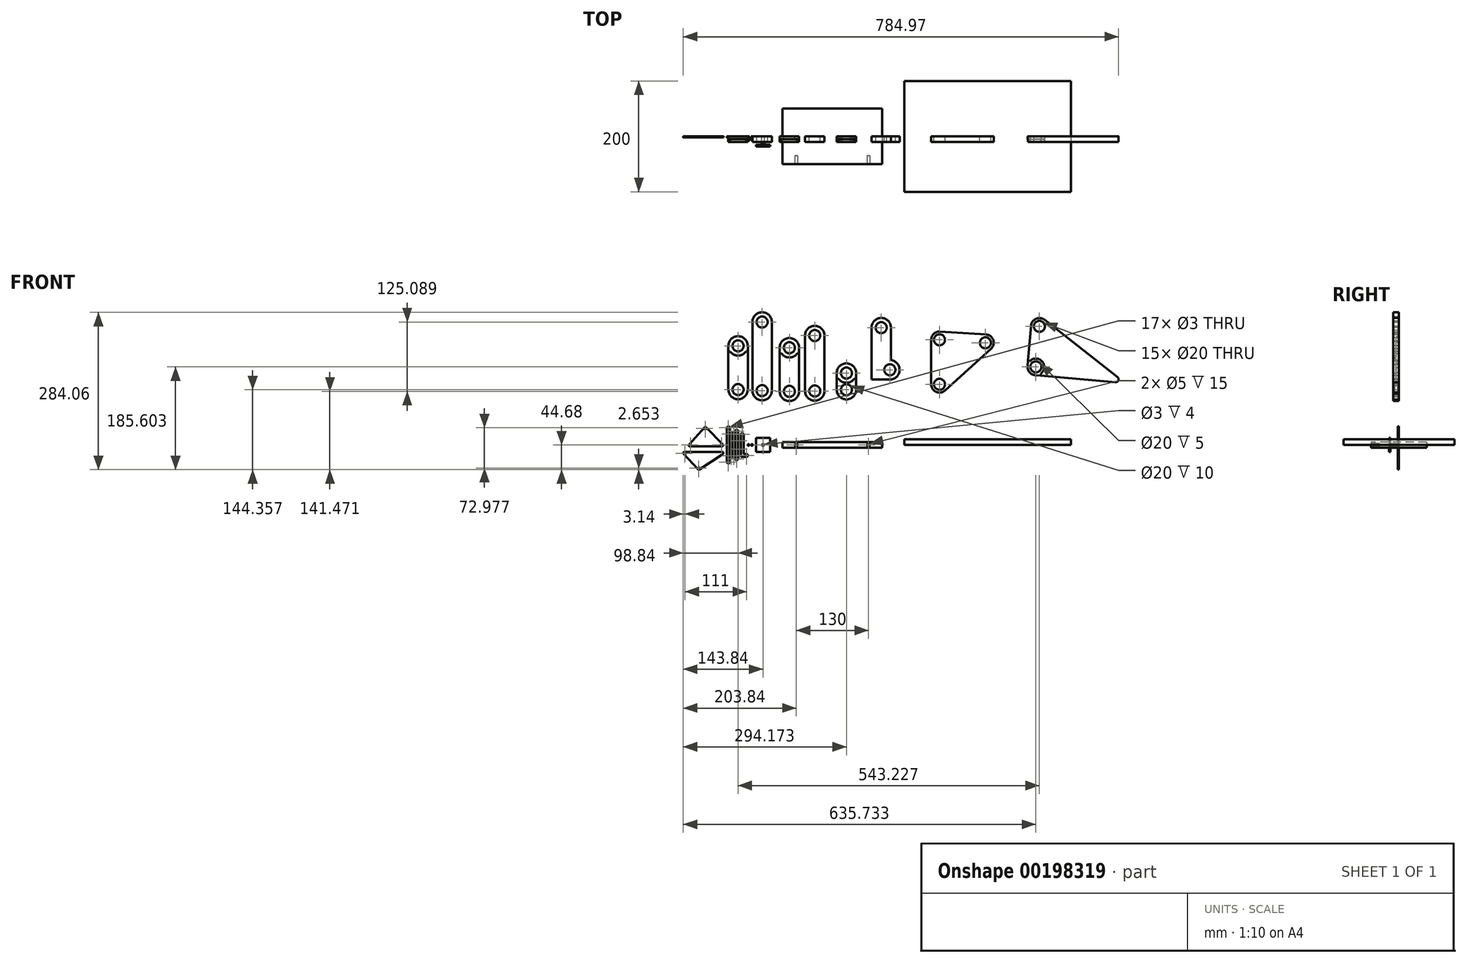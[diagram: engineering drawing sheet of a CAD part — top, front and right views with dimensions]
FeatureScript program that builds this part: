
annotation { "Feature Type Name" : "Feature", "Feature Type Description" : "" }
export const myFeature = defineFeature(function(context is Context, id is Id, definition is map)
    precondition{}
    {
        {
            var Q0;
            Q0=qCreatedBy(makeId("Front.planeOp"),FACE);
            var sketch = newSketch(context, id + "F0", { "sketchPlane" : qUnion([Q0])});
            skLineSegment(sketch, "E0", {"start": v(0, 7.5) * mm, "end": v(0, -7.5) * mm});
            skLineSegment(sketch, "E1", {"start": v(5, 7.5) * mm, "end": v(5, -7.5) * mm});
            skArc(sketch, "E2", {"start": v(5, 7.5) * mm, "mid": v(2.5, 10) * mm, "end": v(0, 7.5) * mm});
            skArc(sketch, "E3", {"start": v(0, -7.5) * mm, "mid": v(2.5, -10) * mm, "end": v(5, -7.5) * mm});
            skCircle(sketch, "E4", {"center": v(2.5, 7.5) * mm, "radius": 1.5 * mm});
            skCircle(sketch, "E5", {"center": v(2.5, -7.5) * mm, "radius": 1.5 * mm});
            skSolve(sketch);
        }
        {
            var Q0;
            Q0=makeQuery(id+"F0.imprint","IMPRINT",FACE,{"disambiguationData":[TD([[makeQuery(id+"F0.imprint","IMPRINT",EDGE,{"derivedFrom":sQuery(id+"F0.wireOp",EDGE,"E0")}),1.0]])]});
            extrude(context, id + "F1", {"entities" : qUnion([Q0]), "depth" : 2 * mm});
        }
        {
            var Q0;
            Q0=qCreatedBy(makeId("Front.planeOp"),FACE);
            var sketch = newSketch(context, id + "F2", { "sketchPlane" : qUnion([Q0])});
            skLineSegment(sketch, "E6", {"start": v(0, 25) * mm, "end": v(0, -25) * mm});
            skLineSegment(sketch, "E7", {"start": v(-5, 25) * mm, "end": v(-5, -25) * mm});
            skArc(sketch, "E8", {"start": v(0, 25) * mm, "mid": v(-2.5, 27.5) * mm, "end": v(-5, 25) * mm});
            skArc(sketch, "E9", {"start": v(-5, -25) * mm, "mid": v(-2.5, -27.5) * mm, "end": v(0, -25) * mm});
            skCircle(sketch, "E10", {"center": v(-2.5, 25) * mm, "radius": 1.5 * mm});
            skCircle(sketch, "E11", {"center": v(-2.5, -25) * mm, "radius": 1.5 * mm});
            skSolve(sketch);
        }
        {
            var Q0;
            Q0=makeQuery(id+"F2.imprint","IMPRINT",FACE,{"disambiguationData":[TD([[makeQuery(id+"F2.imprint","IMPRINT",EDGE,{"derivedFrom":sQuery(id+"F2.wireOp",EDGE,"E6")}),-1.0]])]});
            extrude(context, id + "F3", {"entities" : qUnion([Q0]), "depth" : 2 * mm});
        }
        {
            var Q0;
            Q0=qCreatedBy(makeId("Front.planeOp"),FACE);
            var sketch = newSketch(context, id + "F4", { "sketchPlane" : qUnion([Q0])});
            skLineSegment(sketch, "E12", {"start": v(-5, 19.65) * mm, "end": v(-5, -19.65) * mm});
            skLineSegment(sketch, "E13", {"start": v(-10, 19.65) * mm, "end": v(-10, -19.65) * mm});
            skArc(sketch, "E14", {"start": v(-5, 19.65) * mm, "mid": v(-7.5, 22.15) * mm, "end": v(-10, 19.65) * mm});
            skArc(sketch, "E15", {"start": v(-10, -19.65) * mm, "mid": v(-7.5, -22.15) * mm, "end": v(-5, -19.65) * mm});
            skCircle(sketch, "E16", {"center": v(-7.5, 19.65) * mm, "radius": 1.5 * mm});
            skCircle(sketch, "E17", {"center": v(-7.5, -19.65) * mm, "radius": 1.5 * mm});
            skSolve(sketch);
        }
        {
            var Q0;
            Q0=makeQuery(id+"F4.imprint","IMPRINT",FACE,{"disambiguationData":[TD([[makeQuery(id+"F4.imprint","IMPRINT",EDGE,{"derivedFrom":sQuery(id+"F4.wireOp",EDGE,"E12")}),-1.0]])]});
            extrude(context, id + "F5", {"entities" : qUnion([Q0]), "depth" : 2 * mm});
        }
        {
            var Q0;
            Q0=qCreatedBy(makeId("Front.planeOp"),FACE);
            var sketch = newSketch(context, id + "F6", { "sketchPlane" : qUnion([Q0])});
            skLineSegment(sketch, "E18", {"start": v(-10, 19.7) * mm, "end": v(-10, -19.7) * mm});
            skLineSegment(sketch, "E19", {"start": v(-15, 19.7) * mm, "end": v(-15, -19.7) * mm});
            skArc(sketch, "E20", {"start": v(-10, 19.7) * mm, "mid": v(-12.5, 22.2) * mm, "end": v(-15, 19.7) * mm});
            skArc(sketch, "E21", {"start": v(-15, -19.7) * mm, "mid": v(-12.5, -22.2) * mm, "end": v(-10, -19.7) * mm});
            skCircle(sketch, "E22", {"center": v(-12.5, 19.7) * mm, "radius": 1.5 * mm});
            skCircle(sketch, "E23", {"center": v(-12.5, -19.7) * mm, "radius": 1.5 * mm});
            skSolve(sketch);
        }
        {
            var Q0;
            Q0=makeQuery(id+"F6.imprint","IMPRINT",FACE,{"disambiguationData":[TD([[makeQuery(id+"F6.imprint","IMPRINT",EDGE,{"derivedFrom":sQuery(id+"F6.wireOp",EDGE,"E18")}),-1.0]])]});
            extrude(context, id + "F7", {"entities" : qUnion([Q0]), "depth" : 2 * mm});
        }
        {
            var Q0;
            Q0=qCreatedBy(makeId("Front.planeOp"),FACE);
            var sketch = newSketch(context, id + "F8", { "sketchPlane" : qUnion([Q0])});
            skLineSegment(sketch, "E24", {"start": v(-20, 30.95) * mm, "end": v(-20, -30.95) * mm});
            skLineSegment(sketch, "E25", {"start": v(-15, 30.95) * mm, "end": v(-15, -30.95) * mm});
            skArc(sketch, "E26", {"start": v(-15, 30.95) * mm, "mid": v(-17.5, 33.45) * mm, "end": v(-20, 30.95) * mm});
            skArc(sketch, "E27", {"start": v(-20, -30.95) * mm, "mid": v(-17.5, -33.45) * mm, "end": v(-15, -30.95) * mm});
            skCircle(sketch, "E28", {"center": v(-17.5, -30.95) * mm, "radius": 1.5 * mm});
            skCircle(sketch, "E29", {"center": v(-17.5, 30.95) * mm, "radius": 1.5 * mm});
            skSolve(sketch);
        }
        {
            var Q0;
            Q0=makeQuery(id+"F8.imprint","IMPRINT",FACE,{"disambiguationData":[TD([[makeQuery(id+"F8.imprint","IMPRINT",EDGE,{"derivedFrom":sQuery(id+"F8.wireOp",EDGE,"E24")}),1.0]])]});
            extrude(context, id + "F9", {"entities" : qUnion([Q0]), "depth" : 2 * mm});
        }
        {
            var Q0;
            Q0=qCreatedBy(makeId("Front.planeOp"),FACE);
            var sketch = newSketch(context, id + "F10", { "sketchPlane" : qUnion([Q0])});
            skLineSegment(sketch, "E30", {"start": v(-58.92, 29.76) * mm, "end": v(-30, 0) * mm, "construction": true});
            skLineSegment(sketch, "E31", {"start": v(-30, 0) * mm, "end": v(-85.8, 0) * mm, "construction": true});
            skLineSegment(sketch, "E32", {"start": v(-85.8, 0) * mm, "end": v(-58.92, 29.76) * mm, "construction": true});
            skCircle(sketch, "E33", {"center": v(-85.8, 0) * mm, "radius": 1.5 * mm});
            skCircle(sketch, "E34", {"center": v(-30, 0) * mm, "radius": 1.5 * mm});
            skCircle(sketch, "E35", {"center": v(-58.92, 29.76) * mm, "radius": 1.5 * mm});
            skLineSegment(sketch, "E36", {"start": v(-91.43, -2.5) * mm, "end": v(-24.08, -2.5) * mm});
            skLineSegment(sketch, "E37", {"start": v(-59, 33.42) * mm, "end": v(-91.43, -2.5) * mm});
            skLineSegment(sketch, "E38", {"start": v(-59, 33.42) * mm, "end": v(-24.08, -2.5) * mm});
            skSolve(sketch);
        }
        {
            var Q0;
            Q0=makeQuery(id+"F10.imprint","IMPRINT",FACE,{"disambiguationData":[TD([[makeQuery(id+"F10.imprint","IMPRINT",EDGE,{"derivedFrom":sQuery(id+"F10.wireOp",EDGE,"E33")}),-1.0]])]});
            extrude(context, id + "F11", {"entities" : qUnion([Q0]), "depth" : 2 * mm});
        }
        {
            var Q0;
            Q0=makeQuery(id+"F11.opExtrude","SWEPT_EDGE",EDGE,{"disambiguationData":[OSD([sQuery(id+"F10.wireOp",EDGE,"E36"),sQuery(id+"F10.wireOp",EDGE,"E37")])]});
            var Q1;
            Q1=makeQuery(id+"F11.opExtrude","SWEPT_EDGE",EDGE,{"disambiguationData":[OSD([sQuery(id+"F10.wireOp",EDGE,"E36"),sQuery(id+"F10.wireOp",EDGE,"E38")])]});
            var Q2;
            Q2=makeQuery(id+"F11.opExtrude","SWEPT_EDGE",EDGE,{"disambiguationData":[OSD([sQuery(id+"F10.wireOp",EDGE,"E37"),sQuery(id+"F10.wireOp",EDGE,"E38")])]});
            fillet(context, id + "F12", {"entities" : qUnion([Q0, Q1, Q2]), "radius" : 2 * mm, "tangentPropagation" : true, "allowEdgeOverflow" : false});
        }
        {
            var Q0;
            Q0=qCreatedBy(makeId("Front.planeOp"),FACE);
            var sketch = newSketch(context, id + "F13", { "sketchPlane" : qUnion([Q0])});
            skLineSegment(sketch, "E39", {"start": v(-95.7, -15) * mm, "end": v(-30, -15) * mm, "construction": true});
            skLineSegment(sketch, "E40", {"start": v(-30, -15) * mm, "end": v(-70.87, -42.03) * mm, "construction": true});
            skLineSegment(sketch, "E41", {"start": v(-70.87, -42.03) * mm, "end": v(-95.7, -15) * mm, "construction": true});
            skCircle(sketch, "E42", {"center": v(-95.7, -15) * mm, "radius": 1.5 * mm});
            skCircle(sketch, "E43", {"center": v(-70.87, -42.03) * mm, "radius": 1.5 * mm});
            skLineSegment(sketch, "E44", {"start": v(-101.4, -12.5) * mm, "end": v(-21.69, -12.5) * mm});
            skLineSegment(sketch, "E45", {"start": v(-21.69, -12.5) * mm, "end": v(-71.27, -45.29) * mm});
            skLineSegment(sketch, "E46", {"start": v(-71.27, -45.29) * mm, "end": v(-101.4, -12.5) * mm});
            skSolve(sketch);
        }
        {
            var Q0;
            Q0=makeQuery(id+"F13.imprint","IMPRINT",FACE,{"disambiguationData":[TD([[makeQuery(id+"F13.imprint","IMPRINT",EDGE,{"derivedFrom":sQuery(id+"F13.wireOp",EDGE,"E42")}),-1.0]])]});
            extrude(context, id + "F14", {"entities" : qUnion([Q0]), "depth" : 2 * mm});
        }
        {
            var Q0;
            Q0=makeQuery(id+"F14.opExtrude","SWEPT_EDGE",EDGE,{"disambiguationData":[OSD([sQuery(id+"F13.wireOp",EDGE,"E44"),sQuery(id+"F13.wireOp",EDGE,"E46")])]});
            var Q1;
            Q1=makeQuery(id+"F14.opExtrude","SWEPT_EDGE",EDGE,{"disambiguationData":[OSD([sQuery(id+"F13.wireOp",EDGE,"E45"),sQuery(id+"F13.wireOp",EDGE,"E46")])]});
            var Q2;
            Q2=makeQuery(id+"F14.opExtrude","SWEPT_EDGE",EDGE,{"disambiguationData":[OSD([sQuery(id+"F13.wireOp",EDGE,"E44"),sQuery(id+"F13.wireOp",EDGE,"E45")])]});
            fillet(context, id + "F15", {"entities" : qUnion([Q0, Q1, Q2]), "radius" : 2 * mm, "tangentPropagation" : true, "allowEdgeOverflow" : false});
        }
        {
            var Q0;
            Q0=qCreatedBy(makeId("Front.planeOp"),FACE);
            var sketch = newSketch(context, id + "F16", { "sketchPlane" : qUnion([Q0])});
            skLineSegment(sketch, "E47", {"start": v(7.5, 19) * mm, "end": v(7.5, -19) * mm, "construction": true});
            skLineSegment(sketch, "E48", {"start": v(7.5, -19) * mm, "end": v(15.3, -19) * mm, "construction": true});
            skArc(sketch, "E49", {"start": v(10, 19) * mm, "mid": v(7.5, 21.5) * mm, "end": v(5, 19) * mm});
            skArc(sketch, "E50", {"start": v(15.3, -21.5) * mm, "mid": v(17.8, -19) * mm, "end": v(15.3, -16.5) * mm});
            skLineSegment(sketch, "E51", {"start": v(5, 19) * mm, "end": v(5, -21.5) * mm});
            skLineSegment(sketch, "E52", {"start": v(15.3, -21.5) * mm, "end": v(5, -21.5) * mm});
            skLineSegment(sketch, "E53", {"start": v(10, 19) * mm, "end": v(10, -16.5) * mm});
            skLineSegment(sketch, "E54", {"start": v(15.3, -16.5) * mm, "end": v(10, -16.5) * mm});
            skCircle(sketch, "E55", {"center": v(7.5, 19) * mm, "radius": 1.5 * mm});
            skCircle(sketch, "E56", {"center": v(15.3, -19) * mm, "radius": 1.5 * mm});
            skSolve(sketch);
        }
        {
            var Q0;
            Q0=makeQuery(id+"F16.imprint","IMPRINT",FACE,{"disambiguationData":[TD([[makeQuery(id+"F16.imprint","IMPRINT",EDGE,{"derivedFrom":sQuery(id+"F16.wireOp",EDGE,"E49")}),1.0]])]});
            extrude(context, id + "F17", {"entities" : qUnion([Q0]), "depth" : 2 * mm});
        }
        {
            var Q0;
            Q0=qCreatedBy(makeId("Front.planeOp"),FACE);
            var sketch = newSketch(context, id + "F18", { "sketchPlane" : qUnion([Q0])});
            skCircle(sketch, "E57", {"center": v(24.95, 0) * mm, "radius": 1.5 * mm});
            skSolve(sketch);
        }
        {
            var Q0;
            Q0=makeQuery(id+"F18.imprint","IMPRINT",FACE,{"disambiguationData":[TD([[makeQuery(id+"F18.imprint","IMPRINT",EDGE,{"derivedFrom":sQuery(id+"F18.wireOp",EDGE,"E57")}),1.0]])]});
            extrude(context, id + "F19", {"entities" : qUnion([Q0]), "depth" : 6 * mm});
        }
        {
            var Q0;
            Q0=qCreatedBy(makeId("Front.planeOp"),FACE);
            var sketch = newSketch(context, id + "F20", { "sketchPlane" : qUnion([Q0])});
            skCircle(sketch, "E58", {"center": v(45, 0) * mm, "radius": 2.5 * mm});
            skSolve(sketch);
        }
        {
            var Q0;
            Q0=makeQuery(id+"F20.imprint","IMPRINT",FACE,{"disambiguationData":[TD([[makeQuery(id+"F20.imprint","IMPRINT",EDGE,{"derivedFrom":sQuery(id+"F20.wireOp",EDGE,"E58")}),1.0]])]});
            extrude(context, id + "F21", {"entities" : qUnion([Q0]), "depth" : 15 * mm, "offsetDistance" : 25 * mm});
        }
        {
            var Q0;
            Q0=makeQuery(id+"F21.opExtrude","CAP_FACE",FACE,{"disambiguationData":[OSD([sQuery(id+"F20.wireOp",EDGE,"E58")])],"isStart":false});
            var sketch = newSketch(context, id + "F22", { "sketchPlane" : qUnion([Q0])});
            skLineSegment(sketch, "E59.bottom", {"start": v(32.5, 12.5) * mm, "end": v(57.5, 12.5) * mm});
            skLineSegment(sketch, "E59.top", {"start": v(32.5, -12.5) * mm, "end": v(57.5, -12.5) * mm});
            skLineSegment(sketch, "E59.left", {"start": v(32.5, 12.5) * mm, "end": v(32.5, -12.5) * mm});
            skLineSegment(sketch, "E59.right", {"start": v(57.5, 12.5) * mm, "end": v(57.5, -12.5) * mm});
            skCircle(sketch, "E60.0", {"center": v(45, 0) * mm, "radius": 2.5 * mm, "construction": true});
            skSolve(sketch);
        }
        {
            var Q0;
            Q0=makeQuery(id+"F22.imprint","IMPRINT",FACE,{"disambiguationData":[TD([[makeQuery(id+"F22.imprint","IMPRINT",EDGE,{"derivedFrom":sQuery(id+"F22.wireOp",EDGE,"E59.bottom")}),-1.0]])]});
            var Q1;
            Q1=makeQuery(id+"F22.imprint","IMPRINT",FACE,{"disambiguationData":[TD([[makeQuery(id+"F22.imprint","IMPRINT",EDGE,{"derivedFrom":makeQuery(id+"F21.opExtrude","CAP_EDGE",EDGE,{"disambiguationData":[OSD([sQuery(id+"F20.wireOp",EDGE,"E58")])],"isStart":false})}),1.0]])]});
            extrude(context, id + "F23", {"entities" : qUnion([Q0, Q1]), "operationType" : NewBodyOperationType.ADD, "depth" : 3 * mm});
        }
        {
            var Q0;
            Q0=makeQuery(id+"F23.opExtrude","CAP_FACE",FACE,{"disambiguationData":[OSD([sQuery(id+"F22.wireOp",EDGE,"E59.bottom"),sQuery(id+"F22.wireOp",EDGE,"E59.top"),sQuery(id+"F22.wireOp",EDGE,"E59.left"),sQuery(id+"F22.wireOp",EDGE,"E59.right")])],"isStart":false});
            var sketch = newSketch(context, id + "F24", { "sketchPlane" : qUnion([Q0])});
            skCircle(sketch, "E61", {"center": v(45, 0) * mm, "radius": 1.5 * mm});
            skSolve(sketch);
        }
        {
            var Q0;
            Q0=makeQuery(id+"F24.imprint","IMPRINT",FACE,{"disambiguationData":[TD([[makeQuery(id+"F24.imprint","IMPRINT",EDGE,{"derivedFrom":sQuery(id+"F24.wireOp",EDGE,"E61")}),1.0]])]});
            extrude(context, id + "F25", {"entities" : qUnion([Q0]), "operationType" : NewBodyOperationType.REMOVE, "oppositeDirection" : true, "depth" : 4 * mm});
        }
        {
            var Q0;
            Q0=qCreatedBy(makeId("Front.planeOp"),FACE);
            var sketch = newSketch(context, id + "F26", { "sketchPlane" : qUnion([Q0])});
            skCircle(sketch, "E62", {"center": v(18.95, 0) * mm, "radius": 1.5 * mm});
            skSolve(sketch);
        }
        {
            var Q0;
            Q0=makeQuery(id+"F26.imprint","IMPRINT",FACE,{"disambiguationData":[TD([[makeQuery(id+"F26.imprint","IMPRINT",EDGE,{"derivedFrom":sQuery(id+"F26.wireOp",EDGE,"E62")}),1.0]])]});
            extrude(context, id + "F27", {"entities" : qUnion([Q0]), "depth" : 8 * mm});
        }
        {
            var Q0;
            Q0=qCreatedBy(makeId("Top.planeOp"),FACE);
            var sketch = newSketch(context, id + "F28", { "sketchPlane" : qUnion([Q0])});
            skLineSegment(sketch, "E63.bottom", {"start": v(80, 50) * mm, "end": v(260, 50) * mm});
            skLineSegment(sketch, "E63.top", {"start": v(80, -50) * mm, "end": v(260, -50) * mm});
            skLineSegment(sketch, "E63.left", {"start": v(80, 50) * mm, "end": v(80, -50) * mm});
            skLineSegment(sketch, "E63.right", {"start": v(260, 50) * mm, "end": v(260, -50) * mm});
            skSolve(sketch);
        }
        {
            var Q0;
            Q0 = qSketchRegion(id + "F28", true);
            extrude(context, id + "F29", {"entities" : qUnion([Q0]), "depth" : 5 * mm, "offsetDistance" : 25 * mm, "hasSecondDirection" : true, "secondDirectionOppositeDirection" : true, "secondDirectionDepth" : 5 * mm});
        }
        {
            var Q0;
            Q0=makeQuery(id+"F29.opExtrude","SWEPT_FACE",FACE,{"disambiguationData":[OSD([sQuery(id+"F28.wireOp",EDGE,"E63.top")])]});
            var sketch = newSketch(context, id + "F30", { "sketchPlane" : qUnion([Q0])});
            skCircle(sketch, "E64", {"center": v(105, 0) * mm, "radius": 2.5 * mm});
            skPoint(sketch, "E64.centerSnap0", {"position": v(80, 0) * mm});
            skCircle(sketch, "E65", {"center": v(235, 0) * mm, "radius": 2.5 * mm});
            skSolve(sketch);
        }
        {
            var Q0;
            Q0 = qSketchRegion(id + "F30", true);
            extrude(context, id + "F31", {"entities" : qUnion([Q0]), "operationType" : NewBodyOperationType.REMOVE, "oppositeDirection" : true, "depth" : 15 * mm, "offsetDistance" : 25 * mm});
        }
        {
            var Q0;
            Q0=qCreatedBy(makeId("Top.planeOp"),FACE);
            var sketch = newSketch(context, id + "F32", { "sketchPlane" : qUnion([Q0])});
            skLineSegment(sketch, "E66.bottom", {"start": v(300, 100) * mm, "end": v(600, 100) * mm});
            skLineSegment(sketch, "E66.top", {"start": v(300, -100) * mm, "end": v(600, -100) * mm});
            skLineSegment(sketch, "E66.left", {"start": v(300, 100) * mm, "end": v(300, -100) * mm});
            skLineSegment(sketch, "E66.right", {"start": v(600, 100) * mm, "end": v(600, -100) * mm});
            skSolve(sketch);
        }
        {
            var Q0;
            Q0 = qSketchRegion(id + "F32", true);
            extrude(context, id + "F33", {"entities" : qUnion([Q0]), "depth" : 10 * mm, "offsetDistance" : 25 * mm});
        }
        {
            var Q0;
            Q0=qCreatedBy(makeId("Front.planeOp"),FACE);
            var sketch = newSketch(context, id + "F34", { "sketchPlane" : qUnion([Q0])});
            skCircle(sketch, "E67", {"center": v(0, 178.8) * mm, "radius": 10 * mm});
            skCircle(sketch, "E68", {"center": v(0, 100) * mm, "radius": 10 * mm});
            skArc(sketch, "E69", {"start": v(17.5, 178.8) * mm, "mid": v(0, 196.3) * mm, "end": v(-17.5, 178.8) * mm});
            skArc(sketch, "E70", {"start": v(-17.5, 100) * mm, "mid": v(0, 82.5) * mm, "end": v(17.5, 100) * mm});
            skLineSegment(sketch, "E71", {"start": v(-17.5, 178.8) * mm, "end": v(-17.5, 100) * mm});
            skLineSegment(sketch, "E72", {"start": v(17.5, 178.8) * mm, "end": v(17.5, 100) * mm});
            skSolve(sketch);
        }
        {
            var Q0;
            Q0 = qSketchRegion(id + "F34", true);
            extrude(context, id + "F35", {"entities" : qUnion([Q0]), "depth" : 10 * mm, "offsetDistance" : 25 * mm});
        }
        {
            var Q0;
            Q0=qCreatedBy(makeId("Front.planeOp"),FACE);
            var sketch = newSketch(context, id + "F36", { "sketchPlane" : qUnion([Q0])});
            skCircle(sketch, "E73", {"center": v(43.37, 98.08) * mm, "radius": 10 * mm});
            skArc(sketch, "E74", {"start": v(25.87, 98.08) * mm, "mid": v(43.37, 80.58) * mm, "end": v(60.87, 98.08) * mm});
            skArc(sketch, "E75", {"start": v(60.87, 221.88) * mm, "mid": v(43.37, 239.38) * mm, "end": v(25.87, 221.88) * mm});
            skCircle(sketch, "E76", {"center": v(43.37, 221.88) * mm, "radius": 10 * mm});
            skLineSegment(sketch, "E77", {"start": v(25.87, 221.88) * mm, "end": v(25.87, 98.08) * mm});
            skLineSegment(sketch, "E78", {"start": v(60.87, 221.88) * mm, "end": v(60.87, 98.08) * mm});
            skSolve(sketch);
        }
        {
            var Q0;
            Q0 = qSketchRegion(id + "F36", true);
            extrude(context, id + "F37", {"entities" : qUnion([Q0]), "depth" : 10 * mm, "offsetDistance" : 25 * mm});
        }
        {
            var Q0;
            Q0=qCreatedBy(makeId("Front.planeOp"),FACE);
            var sketch = newSketch(context, id + "F38", { "sketchPlane" : qUnion([Q0])});
            skCircle(sketch, "E79", {"center": v(92.5, 96.8) * mm, "radius": 10 * mm});
            skCircle(sketch, "E80", {"center": v(92.5, 175.4) * mm, "radius": 10 * mm});
            skArc(sketch, "E81", {"start": v(110, 175.4) * mm, "mid": v(92.5, 192.9) * mm, "end": v(75, 175.4) * mm});
            skArc(sketch, "E82", {"start": v(75, 96.8) * mm, "mid": v(92.5, 79.3) * mm, "end": v(110, 96.8) * mm});
            skLineSegment(sketch, "E83", {"start": v(75, 175.4) * mm, "end": v(75, 96.8) * mm});
            skLineSegment(sketch, "E84", {"start": v(110, 175.4) * mm, "end": v(110, 96.8) * mm});
            skSolve(sketch);
        }
        {
            var Q0;
            Q0 = qSketchRegion(id + "F38", true);
            extrude(context, id + "F39", {"entities" : qUnion([Q0]), "depth" : 10 * mm, "offsetDistance" : 25 * mm});
        }
        {
            var Q0;
            Q0=qCreatedBy(makeId("Front.planeOp"),FACE);
            var sketch = newSketch(context, id + "F40", { "sketchPlane" : qUnion([Q0])});
            skCircle(sketch, "E85", {"center": v(138.24, 97.46) * mm, "radius": 10 * mm});
            skCircle(sketch, "E86", {"center": v(138.24, 197.46) * mm, "radius": 10 * mm});
            skArc(sketch, "E87", {"start": v(155.74, 197.46) * mm, "mid": v(138.24, 214.96) * mm, "end": v(120.74, 197.46) * mm});
            skArc(sketch, "E88", {"start": v(120.74, 97.46) * mm, "mid": v(138.24, 79.96) * mm, "end": v(155.74, 97.46) * mm});
            skLineSegment(sketch, "E89", {"start": v(120.74, 197.46) * mm, "end": v(120.74, 97.46) * mm});
            skLineSegment(sketch, "E90", {"start": v(155.74, 197.46) * mm, "end": v(155.74, 97.46) * mm});
            skSolve(sketch);
        }
        {
            var Q0;
            Q0 = qSketchRegion(id + "F40", true);
            extrude(context, id + "F41", {"entities" : qUnion([Q0]), "depth" : 10 * mm, "offsetDistance" : 25 * mm});
        }
        {
            var Q0;
            Q0=qCreatedBy(makeId("Front.planeOp"),FACE);
            var sketch = newSketch(context, id + "F42", { "sketchPlane" : qUnion([Q0])});
            skCircle(sketch, "E91", {"center": v(195.33, 99.68) * mm, "radius": 10 * mm});
            skCircle(sketch, "E92", {"center": v(195.33, 129.68) * mm, "radius": 10 * mm});
            skArc(sketch, "E93", {"start": v(212.83, 129.68) * mm, "mid": v(195.33, 147.18) * mm, "end": v(177.83, 129.68) * mm});
            skArc(sketch, "E94", {"start": v(177.83, 99.68) * mm, "mid": v(195.33, 82.18) * mm, "end": v(212.83, 99.68) * mm});
            skLineSegment(sketch, "E95", {"start": v(177.83, 129.68) * mm, "end": v(177.83, 99.68) * mm});
            skLineSegment(sketch, "E96", {"start": v(212.83, 129.68) * mm, "end": v(212.83, 99.68) * mm});
            skSolve(sketch);
        }
        {
            var Q0;
            Q0 = qSketchRegion(id + "F42", true);
            extrude(context, id + "F43", {"entities" : qUnion([Q0]), "depth" : 10 * mm, "offsetDistance" : 25 * mm});
        }
        {
            var Q0;
            Q0=qCreatedBy(makeId("Front.planeOp"),FACE);
            var sketch = newSketch(context, id + "F44", { "sketchPlane" : qUnion([Q0])});
            skLineSegment(sketch, "E97", {"start": v(258.08, 211.66) * mm, "end": v(258.08, 135.66) * mm, "construction": true});
            skLineSegment(sketch, "E98", {"start": v(258.08, 135.66) * mm, "end": v(273.68, 135.66) * mm, "construction": true});
            skCircle(sketch, "E99", {"center": v(258.08, 211.66) * mm, "radius": 10 * mm});
            skCircle(sketch, "E100", {"center": v(273.68, 135.66) * mm, "radius": 10 * mm});
            skArc(sketch, "E101", {"start": v(275.58, 211.66) * mm, "mid": v(258.08, 229.16) * mm, "end": v(240.58, 211.66) * mm});
            skArc(sketch, "E102", {"start": v(273.68, 118.16) * mm, "mid": v(291.15, 134.7) * mm, "end": v(275.58, 153.05) * mm});
            skLineSegment(sketch, "E103", {"start": v(275.58, 211.66) * mm, "end": v(275.58, 153.05) * mm});
            skLineSegment(sketch, "E104", {"start": v(240.58, 211.66) * mm, "end": v(240.58, 118.16) * mm});
            skLineSegment(sketch, "E105", {"start": v(240.58, 118.16) * mm, "end": v(273.68, 118.16) * mm});
            skSolve(sketch);
        }
        {
            var Q0;
            Q0 = qSketchRegion(id + "F44", true);
            extrude(context, id + "F45", {"entities" : qUnion([Q0]), "depth" : 10 * mm, "offsetDistance" : 25 * mm});
        }
        {
            var Q0;
            Q0=qCreatedBy(makeId("Front.planeOp"),FACE);
            var sketch = newSketch(context, id + "F46", { "sketchPlane" : qUnion([Q0])});
            skLineSegment(sketch, "E106", {"start": v(363.12, 189.73) * mm, "end": v(363.12, 109.53) * mm, "construction": true});
            skLineSegment(sketch, "E107", {"start": v(363.12, 109.53) * mm, "end": v(445.94, 184.33) * mm, "construction": true});
            skLineSegment(sketch, "E108", {"start": v(445.94, 184.33) * mm, "end": v(363.12, 189.73) * mm, "construction": true});
            skCircle(sketch, "E109", {"center": v(363.12, 189.73) * mm, "radius": 10 * mm});
            skCircle(sketch, "E110", {"center": v(445.94, 184.33) * mm, "radius": 10 * mm});
            skCircle(sketch, "E111", {"center": v(363.12, 109.53) * mm, "radius": 10 * mm});
            skArc(sketch, "E112", {"start": v(364.1, 204.7) * mm, "mid": v(352.86, 200.68) * mm, "end": v(348.12, 189.73) * mm});
            skLineSegment(sketch, "E113", {"start": v(348.12, 189.73) * mm, "end": v(348.12, 109.53) * mm});
            skLineSegment(sketch, "E114.0", {"start": v(446.92, 199.3) * mm, "end": v(364.1, 204.7) * mm});
            skLineSegment(sketch, "E114.1", {"start": v(373.17, 98.4) * mm, "end": v(456, 173.2) * mm});
            skPoint(sketch, "E115.visualSharp", {"position": v(482.34, 196.98) * mm});
            skArc(sketch, "E115.filletArc", {"start": v(456, 173.2) * mm, "mid": v(460.1, 189.25) * mm, "end": v(446.92, 199.3) * mm});
            skArc(sketch, "E116", {"start": v(348.12, 109.53) * mm, "mid": v(357.02, 95.82) * mm, "end": v(373.17, 98.4) * mm});
            skSolve(sketch);
        }
        {
            var Q0;
            Q0 = qSketchRegion(id + "F46", true);
            extrude(context, id + "F47", {"entities" : qUnion([Q0]), "depth" : 10 * mm, "offsetDistance" : 25 * mm});
        }
        {
            var Q0;
            Q0=qCreatedBy(makeId("Front.planeOp"),FACE);
            var sketch = newSketch(context, id + "F48", { "sketchPlane" : qUnion([Q0])});
            skLineSegment(sketch, "E117", {"start": v(536.9, 140.92) * mm, "end": v(543.23, 214.05) * mm, "construction": true});
            skLineSegment(sketch, "E118", {"start": v(543.23, 214.05) * mm, "end": v(648.58, 131.25) * mm, "construction": true});
            skLineSegment(sketch, "E119", {"start": v(648.58, 131.25) * mm, "end": v(536.9, 140.92) * mm, "construction": true});
            skCircle(sketch, "E120", {"center": v(543.23, 214.05) * mm, "radius": 10 * mm});
            skCircle(sketch, "E121", {"center": v(536.9, 140.92) * mm, "radius": 10 * mm});
            skArc(sketch, "E122", {"start": v(552.5, 225.84) * mm, "mid": v(537.26, 227.81) * mm, "end": v(528.28, 215.34) * mm});
            skArc(sketch, "E123", {"start": v(521.95, 142.22) * mm, "mid": v(525.41, 131.27) * mm, "end": v(535.6, 125.98) * mm});
            skLineSegment(sketch, "E124", {"start": v(536.9, 140.92) * mm, "end": v(467.82, 146.9) * mm, "construction": true});
            skLineSegment(sketch, "E125", {"start": v(521.95, 142.22) * mm, "end": v(528.28, 215.34) * mm});
            skLineSegment(sketch, "E126", {"start": v(535.6, 125.98) * mm, "end": v(680.7, 113.41) * mm});
            skLineSegment(sketch, "E127", {"start": v(552.5, 225.84) * mm, "end": v(684.22, 122.32) * mm});
            skPoint(sketch, "E128.visualSharp", {"position": v(697.4, 111.97) * mm});
            skArc(sketch, "E128.filletArc", {"start": v(680.7, 113.41) * mm, "mid": v(685.78, 116.56) * mm, "end": v(684.22, 122.32) * mm});
            skSolve(sketch);
        }
        {
            var Q0;
            Q0 = qSketchRegion(id + "F48", true);
            extrude(context, id + "F49", {"entities" : qUnion([Q0]), "depth" : 10 * mm, "offsetDistance" : 25 * mm});
        }
        {
            var Q0;
            Q0=makeQuery(id+"F35.opExtrude","CAP_FACE",FACE,{"disambiguationData":[OSD([sQuery(id+"F34.wireOp",EDGE,"E67"),sQuery(id+"F34.wireOp",EDGE,"E68"),sQuery(id+"F34.wireOp",EDGE,"E69"),sQuery(id+"F34.wireOp",EDGE,"E70"),sQuery(id+"F34.wireOp",EDGE,"E71"),sQuery(id+"F34.wireOp",EDGE,"E72")])],"isStart":false});
            var sketch = newSketch(context, id + "F50", { "sketchPlane" : qUnion([Q0])});
            skArc(sketch, "E129", {"start": v(-14.36, 168.8) * mm, "mid": v(0, 161.3) * mm, "end": v(14.36, 168.8) * mm});
            skLineSegment(sketch, "E130", {"start": v(-14.36, 168.8) * mm, "end": v(-17.5, 168.8) * mm});
            skLineSegment(sketch, "E131", {"start": v(14.36, 168.8) * mm, "end": v(17.5, 168.8) * mm});
            skLineSegment(sketch, "E132", {"start": v(-17.5, 168.8) * mm, "end": v(-17.5, 178.8) * mm});
            skLineSegment(sketch, "E133", {"start": v(17.5, 168.8) * mm, "end": v(17.5, 178.8) * mm});
            skArc(sketch, "E134.trimOffspring", {"start": v(17.5, 178.8) * mm, "mid": v(0, 196.3) * mm, "end": v(-17.5, 178.8) * mm});
            skSolve(sketch);
        }
        {
            var Q0;
            Q0 = qSketchRegion(id + "F50", true);
            extrude(context, id + "F51", {"entities" : qUnion([Q0]), "operationType" : NewBodyOperationType.REMOVE, "oppositeDirection" : true, "depth" : 5 * mm, "offsetDistance" : 25 * mm});
        }
        {
            var Q0;
            Q0=makeQuery(id+"F43.opExtrude","CAP_FACE",FACE,{"disambiguationData":[OSD([sQuery(id+"F42.wireOp",EDGE,"E91"),sQuery(id+"F42.wireOp",EDGE,"E92"),sQuery(id+"F42.wireOp",EDGE,"E93"),sQuery(id+"F42.wireOp",EDGE,"E94"),sQuery(id+"F42.wireOp",EDGE,"E95"),sQuery(id+"F42.wireOp",EDGE,"E96")])],"isStart":false});
            var sketch = newSketch(context, id + "F52", { "sketchPlane" : qUnion([Q0])});
            skArc(sketch, "E135", {"start": v(180.97, 119.68) * mm, "mid": v(195.33, 112.18) * mm, "end": v(209.7, 119.68) * mm});
            skLineSegment(sketch, "E136", {"start": v(177.83, 119.68) * mm, "end": v(180.97, 119.68) * mm});
            skLineSegment(sketch, "E137", {"start": v(209.7, 119.68) * mm, "end": v(212.83, 119.68) * mm});
            skLineSegment(sketch, "E138", {"start": v(177.83, 129.68) * mm, "end": v(177.83, 119.68) * mm});
            skLineSegment(sketch, "E139", {"start": v(212.83, 119.68) * mm, "end": v(212.83, 129.68) * mm});
            skArc(sketch, "E140.trimOffspring", {"start": v(212.83, 129.68) * mm, "mid": v(195.33, 147.18) * mm, "end": v(177.83, 129.68) * mm});
            skSolve(sketch);
        }
        {
            var Q0;
            Q0 = qSketchRegion(id + "F52", true);
            extrude(context, id + "F53", {"entities" : qUnion([Q0]), "operationType" : NewBodyOperationType.REMOVE, "oppositeDirection" : true, "depth" : 5 * mm, "offsetDistance" : 25 * mm});
        }
        {
            var Q0;
            Q0=makeQuery(id+"F39.opExtrude","CAP_FACE",FACE,{"disambiguationData":[OSD([sQuery(id+"F38.wireOp",EDGE,"E79"),sQuery(id+"F38.wireOp",EDGE,"E80"),sQuery(id+"F38.wireOp",EDGE,"E81"),sQuery(id+"F38.wireOp",EDGE,"E82"),sQuery(id+"F38.wireOp",EDGE,"E83"),sQuery(id+"F38.wireOp",EDGE,"E84")])],"isStart":false});
            var sketch = newSketch(context, id + "F54", { "sketchPlane" : qUnion([Q0])});
            skArc(sketch, "E141", {"start": v(78.14, 165.4) * mm, "mid": v(92.5, 157.9) * mm, "end": v(106.87, 165.4) * mm});
            skLineSegment(sketch, "E142", {"start": v(75, 165.4) * mm, "end": v(78.14, 165.4) * mm});
            skLineSegment(sketch, "E143.trimOffspring", {"start": v(106.87, 165.4) * mm, "end": v(110, 165.4) * mm});
            skLineSegment(sketch, "E144", {"start": v(75, 165.4) * mm, "end": v(75, 175.4) * mm});
            skLineSegment(sketch, "E145", {"start": v(110, 165.4) * mm, "end": v(110, 175.4) * mm});
            skArc(sketch, "E146.trimOffspring", {"start": v(110, 175.4) * mm, "mid": v(92.5, 192.9) * mm, "end": v(75, 175.4) * mm});
            skSolve(sketch);
        }
        {
            var Q0;
            Q0 = qSketchRegion(id + "F54", true);
            extrude(context, id + "F55", {"entities" : qUnion([Q0]), "operationType" : NewBodyOperationType.REMOVE, "oppositeDirection" : true, "depth" : 5 * mm, "offsetDistance" : 25 * mm});
        }
        {
            var Q0;
            Q0=makeQuery(id+"F49.opExtrude","CAP_FACE",FACE,{"disambiguationData":[OSD([sQuery(id+"F48.wireOp",EDGE,"E120"),sQuery(id+"F48.wireOp",EDGE,"E121"),sQuery(id+"F48.wireOp",EDGE,"E122"),sQuery(id+"F48.wireOp",EDGE,"E123"),sQuery(id+"F48.wireOp",EDGE,"E125"),sQuery(id+"F48.wireOp",EDGE,"E126"),sQuery(id+"F48.wireOp",EDGE,"E127"),sQuery(id+"F48.wireOp",EDGE,"E128.filletArc")])],"isStart":false});
            var sketch = newSketch(context, id + "F56", { "sketchPlane" : qUnion([Q0])});
            skArc(sketch, "E147", {"start": v(521.95, 142.22) * mm, "mid": v(525.41, 131.27) * mm, "end": v(535.6, 125.98) * mm});
            skLineSegment(sketch, "E148", {"start": v(526.62, 151.85) * mm, "end": v(522.81, 152.18) * mm});
            skLineSegment(sketch, "E149", {"start": v(522.81, 152.18) * mm, "end": v(521.95, 142.22) * mm});
            skLineSegment(sketch, "E150", {"start": v(545.9, 128.92) * mm, "end": v(545.56, 125.12) * mm});
            skLineSegment(sketch, "E151", {"start": v(535.6, 125.98) * mm, "end": v(545.56, 125.12) * mm});
            skArc(sketch, "E152.trimOffspring", {"start": v(545.9, 128.92) * mm, "mid": v(548.38, 150.58) * mm, "end": v(526.62, 151.85) * mm});
            skSolve(sketch);
        }
        {
            var Q0;
            Q0 = qSketchRegion(id + "F56", true);
            extrude(context, id + "F57", {"entities" : qUnion([Q0]), "operationType" : NewBodyOperationType.REMOVE, "oppositeDirection" : true, "depth" : 5 * mm, "offsetDistance" : 25 * mm});
        }
        {
            var Q0;
            Q0=makeQuery(id+"F43.opExtrude","CAP_FACE",FACE,{"disambiguationData":[OSD([sQuery(id+"F42.wireOp",EDGE,"E91"),sQuery(id+"F42.wireOp",EDGE,"E92"),sQuery(id+"F42.wireOp",EDGE,"E93"),sQuery(id+"F42.wireOp",EDGE,"E94"),sQuery(id+"F42.wireOp",EDGE,"E95"),sQuery(id+"F42.wireOp",EDGE,"E96")])],"isStart":false});
            cPlane(context, id + "F58", {"entities" : qUnion([Q0]), "cplaneType" : CPlaneType.OFFSET, "offset" : 5 * mm, "oppositeDirection" : true, "width" : 150 * mm, "height" : 150 * mm});
        }
        {
            var Q0;
            Q0=qCreatedBy(id+"F58.planeOp",FACE);
            var sketch = newSketch(context, id + "F59", { "sketchPlane" : qUnion([Q0])});
            skLineSegment(sketch, "E153.bottom", {"start": v(170.34, 106.68) * mm, "end": v(225.77, 106.68) * mm});
            skLineSegment(sketch, "E153.top", {"start": v(170.34, 92.68) * mm, "end": v(225.77, 92.68) * mm});
            skLineSegment(sketch, "E153.left", {"start": v(170.34, 106.68) * mm, "end": v(170.34, 92.68) * mm});
            skLineSegment(sketch, "E153.right", {"start": v(225.77, 106.68) * mm, "end": v(225.77, 92.68) * mm});
            skCircle(sketch, "E154.0", {"center": v(195.33, 99.68) * mm, "radius": 10 * mm, "construction": true});
            skSolve(sketch);
        }
        {
            var Q0;
            Q0 = qSketchRegion(id + "F59", true);
            extrude(context, id + "F60", {"entities" : qUnion([Q0]), "operationType" : NewBodyOperationType.REMOVE, "oppositeDirection" : true, "depth" : 2.5 * mm, "offsetDistance" : 25 * mm, "hasSecondDirection" : true, "secondDirectionOppositeDirection" : false, "secondDirectionDepth" : 2.5 * mm});
        }
    });
